# Revit family: Cooking_module_4_no of slots
name_source: partatom
category: Generic Models
revit_build: Autodesk Revit Architecture 2013 (Build: 20120221_2030(x64)
units: mm (PartAtom-declared; Revit-internal decimal feet)

## types (8) — shared parameters
D- benchtop = 700.01 mm
D- side box = 100 mm  [stored 0.328084 ft]
D- toe recess offset = 50 mm  [stored 0.164042 ft]
D-cooktop1 = 504.01 mm
D-cooktop2 = 504.01 mm
D-cooktop3 = 504.01 mm
D-cooktop4 = 504.01 mm
H- backpanel offset = 150 mm
H- benchtop = 900 mm
H- bottom of hood = 700 mm
H- total upto cabinets = 2100 mm
H-toe recess = 100 mm  [stored 0.328084 ft]
SS edging = BA-01
T- benchtop = 80 mm
W- back panel offset = 150 mm
W- benchtop waterfall = 80 mm
W- oven1 = 695 mm
W-hood3 cabinet = 1200 mm
W-oven2 = 695 mm
W-oven3 = 695 mm
W-oven4 = 695 mm
W-side box = 150 mm
back panel = PT-02
hood cabinets = PT-01
infills btwn ovens = PT-03
mdf = MDF
side boxes = PT-01
ss infills under oven = SS-01
toe recess = PT-03
waterfalls = PT-03

## per-type parameters (varying)
- Cooking_module_4: D-hood1 C/O=112.6 mm  [stored 0.369423 ft]; D-hood1 C/O offset from backpanel=200 mm  [stored 0.656168 ft]; D-hood1 cabinet=100 mm  [stored 0.328084 ft]; D-hood2 C/O=111.92 mm; D-hood2 C/O offset from backpanel=100 mm  [stored 0.328084 ft]; D-hood2 cabinet=100 mm  [stored 0.328084 ft]; D-hood3 C/O=184.92 mm; D-hood3 C/O offset from backpanel=100 mm  [stored 0.328084 ft]; D-hood3 cabinet=100 mm  [stored 0.328084 ft]; D-hood4 C/O=227.1 mm; D-hood4 C/O offset from backpanel=100 mm  [stored 0.328084 ft]; D-hood4 cabinet=100 mm  [stored 0.328084 ft]; H-oven1=603 mm; H-oven2=603 mm; H-oven3=603 mm; H-oven4=603 mm; No. of slots=0; W- benchtop=1205 mm  [stored 3.95341 ft]; W- offset oven1 frm benchtop left edge=252.5 mm; W-cooktop1=780 mm  [stored 2.55906 ft]; W-cooktop2=780 mm  [stored 2.55906 ft]; W-cooktop3=780 mm  [stored 2.55906 ft]; W-cooktop4=780 mm  [stored 2.55906 ft]; W-hood 2 cabinet=1200 mm; W-hood1 C/O=198.49 mm; W-hood1 cabinet=1200 mm; W-hood2 C/O=251.33 mm; W-hood3 C/O=280 mm; W-hood4 C/O=305.53 mm; W-offset slot2 frm benchtop left edge=1452.5 mm; W-offset slot3 frm bechtop left edge=2652.5 mm; W-offset slot4 frm benchtop left edge=3852.5 mm; inbuilt hood1=No; inbuilt hood2=No; inbuilt hood3=No; inbuilt hood4=No
- Cooking_module_4 2 2: D-hood1 C/O=112.3 mm; D-hood1 C/O offset from backpanel=200 mm  [stored 0.656168 ft]; D-hood1 cabinet=600 mm; D-hood2 C/O=111.92 mm; D-hood2 C/O offset from backpanel=200 mm  [stored 0.656168 ft]; D-hood2 cabinet=600 mm; D-hood3 C/O=184.92 mm; D-hood3 C/O offset from backpanel=100 mm  [stored 0.328084 ft]; D-hood3 cabinet=100 mm  [stored 0.328084 ft]; D-hood4 C/O=227.1 mm; D-hood4 C/O offset from backpanel=100 mm  [stored 0.328084 ft]; D-hood4 cabinet=100 mm  [stored 0.328084 ft]; H-oven1=596 mm; H-oven2=596 mm; H-oven3=596 mm; H-oven4=596 mm; No. of slots=0; W- benchtop=1205 mm  [stored 3.95341 ft]; W- offset oven1 frm benchtop left edge=243.26 mm; W-cooktop1=614 mm  [stored 2.01444 ft]; W-cooktop2=614 mm  [stored 2.01444 ft]; W-cooktop3=614 mm  [stored 2.01444 ft]; W-cooktop4=614 mm  [stored 2.01444 ft]; W-hood 2 cabinet=1200 mm; W-hood1 C/O=198.49 mm; W-hood1 cabinet=1200 mm; W-hood2 C/O=251.33 mm; W-hood3 C/O=280 mm; W-hood4 C/O=305.53 mm; W-offset slot2 frm benchtop left edge=1450 mm  [stored 4.75722 ft]; W-offset slot3 frm bechtop left edge=2652.5 mm; W-offset slot4 frm benchtop left edge=243 mm; inbuilt hood1=Yes; inbuilt hood2=Yes; inbuilt hood3=No; inbuilt hood4=No
- Cooking_module_4 3: D-hood1 C/O=372 mm  [stored 1.22047 ft]; D-hood1 C/O offset from backpanel=181 mm  [stored 0.593832 ft]; D-hood1 cabinet=100 mm  [stored 0.328084 ft]; D-hood2 C/O=372 mm  [stored 1.22047 ft]; D-hood2 C/O offset from backpanel=181 mm  [stored 0.593832 ft]; D-hood2 cabinet=100 mm  [stored 0.328084 ft]; D-hood3 C/O=372 mm  [stored 1.22047 ft]; D-hood3 C/O offset from backpanel=181 mm  [stored 0.593832 ft]; D-hood3 cabinet=100 mm  [stored 0.328084 ft]; D-hood4 C/O=372 mm  [stored 1.22047 ft]; D-hood4 C/O offset from backpanel=181 mm  [stored 0.593832 ft]; D-hood4 cabinet=100 mm  [stored 0.328084 ft]; H-oven1=603 mm; H-oven2=603 mm; H-oven3=603 mm; H-oven4=603 mm; No. of slots=2; W- benchtop=2405 mm; W- offset oven1 frm benchtop left edge=252.5 mm; W-cooktop1=780 mm  [stored 2.55906 ft]; W-cooktop2=780 mm  [stored 2.55906 ft]; W-cooktop3=780 mm  [stored 2.55906 ft]; W-cooktop4=780 mm  [stored 2.55906 ft]; W-hood 2 cabinet=1200 mm; W-hood1 C/O=532 mm  [stored 1.74541 ft]; W-hood1 cabinet=1200 mm; W-hood2 C/O=532 mm  [stored 1.74541 ft]; W-hood3 C/O=532 mm  [stored 1.74541 ft]; W-hood4 C/O=532 mm  [stored 1.74541 ft]; W-offset slot2 frm benchtop left edge=1452.5 mm; W-offset slot3 frm bechtop left edge=2652.5 mm; W-offset slot4 frm benchtop left edge=3852.5 mm; inbuilt hood1=No; inbuilt hood2=No; inbuilt hood3=No; inbuilt hood4=No
- Cooking_module_4 2: D-hood1 C/O=112.3 mm; D-hood1 C/O offset from backpanel=200 mm  [stored 0.656168 ft]; D-hood1 cabinet=100 mm  [stored 0.328084 ft]; D-hood2 C/O=111.92 mm; D-hood2 C/O offset from backpanel=200 mm  [stored 0.656168 ft]; D-hood2 cabinet=100 mm  [stored 0.328084 ft]; D-hood3 C/O=184.92 mm; D-hood3 C/O offset from backpanel=100 mm  [stored 0.328084 ft]; D-hood3 cabinet=100 mm  [stored 0.328084 ft]; D-hood4 C/O=227.1 mm; D-hood4 C/O offset from backpanel=100 mm  [stored 0.328084 ft]; D-hood4 cabinet=100 mm  [stored 0.328084 ft]; H-oven1=596 mm; H-oven2=596 mm; H-oven3=596 mm; H-oven4=596 mm; No. of slots=0; W- benchtop=1205 mm  [stored 3.95341 ft]; W- offset oven1 frm benchtop left edge=243.26 mm; W-cooktop1=614 mm  [stored 2.01444 ft]; W-cooktop2=614 mm  [stored 2.01444 ft]; W-cooktop3=614 mm  [stored 2.01444 ft]; W-cooktop4=614 mm  [stored 2.01444 ft]; W-hood 2 cabinet=1200 mm; W-hood1 C/O=198.49 mm; W-hood1 cabinet=1197.5 mm  [stored 3.92881 ft]; W-hood2 C/O=251.33 mm; W-hood3 C/O=280 mm; W-hood4 C/O=305.53 mm; W-offset slot2 frm benchtop left edge=1451.83 mm  [stored 4.76322 ft]; W-offset slot3 frm bechtop left edge=2652.5 mm; W-offset slot4 frm benchtop left edge=243 mm; inbuilt hood1=No; inbuilt hood2=No; inbuilt hood3=No; inbuilt hood4=No
- Cooking_module_4 2 4: D-hood1 C/O=112.3 mm; D-hood1 C/O offset from backpanel=200 mm  [stored 0.656168 ft]; D-hood1 cabinet=600 mm; D-hood2 C/O=400 mm  [stored 1.31234 ft]; D-hood2 C/O offset from backpanel=180 mm  [stored 0.590551 ft]; D-hood2 cabinet=100 mm  [stored 0.328084 ft]; D-hood3 C/O=184.92 mm; D-hood3 C/O offset from backpanel=100 mm  [stored 0.328084 ft]; D-hood3 cabinet=100 mm  [stored 0.328084 ft]; D-hood4 C/O=227.1 mm; D-hood4 C/O offset from backpanel=100 mm  [stored 0.328084 ft]; D-hood4 cabinet=100 mm  [stored 0.328084 ft]; H-oven1=596 mm; H-oven2=596 mm; H-oven3=596 mm; H-oven4=596 mm; No. of slots=0; W- benchtop=1205 mm  [stored 3.95341 ft]; W- offset oven1 frm benchtop left edge=243.26 mm; W-cooktop1=614 mm  [stored 2.01444 ft]; W-cooktop2=614 mm  [stored 2.01444 ft]; W-cooktop3=614 mm  [stored 2.01444 ft]; W-cooktop4=614 mm  [stored 2.01444 ft]; W-hood 2 cabinet=1200 mm; W-hood1 C/O=198.49 mm; W-hood1 cabinet=1197.5 mm  [stored 3.92881 ft]; W-hood2 C/O=500 mm  [stored 1.64042 ft]; W-hood3 C/O=280 mm; W-hood4 C/O=305.53 mm; W-offset slot2 frm benchtop left edge=1451.83 mm  [stored 4.76322 ft]; W-offset slot3 frm bechtop left edge=2652.5 mm; W-offset slot4 frm benchtop left edge=1451.83 mm  [stored 4.76322 ft]; inbuilt hood1=Yes; inbuilt hood2=No; inbuilt hood3=No; inbuilt hood4=No
- Cooking_module_4 2 3: D-hood1 C/O=112.3 mm; D-hood1 C/O offset from backpanel=200 mm  [stored 0.656168 ft]; D-hood1 cabinet=600 mm; D-hood2 C/O=111.92 mm; D-hood2 C/O offset from backpanel=200 mm  [stored 0.656168 ft]; D-hood2 cabinet=600 mm; D-hood3 C/O=184.92 mm; D-hood3 C/O offset from backpanel=100 mm  [stored 0.328084 ft]; D-hood3 cabinet=600 mm; D-hood4 C/O=227.1 mm; D-hood4 C/O offset from backpanel=100 mm  [stored 0.328084 ft]; D-hood4 cabinet=600 mm; H-oven1=596 mm; H-oven2=596 mm; H-oven3=596 mm; H-oven4=596 mm; No. of slots=0; W- benchtop=1205 mm  [stored 3.95341 ft]; W- offset oven1 frm benchtop left edge=243.26 mm; W-cooktop1=614 mm  [stored 2.01444 ft]; W-cooktop2=614 mm  [stored 2.01444 ft]; W-cooktop3=614 mm  [stored 2.01444 ft]; W-cooktop4=614 mm  [stored 2.01444 ft]; W-hood 2 cabinet=1200 mm; W-hood1 C/O=198.49 mm; W-hood1 cabinet=1197.5 mm  [stored 3.92881 ft]; W-hood2 C/O=251.33 mm; W-hood3 C/O=280 mm; W-hood4 C/O=305.53 mm; W-offset slot2 frm benchtop left edge=1451.83 mm  [stored 4.76322 ft]; W-offset slot3 frm bechtop left edge=2652.5 mm; W-offset slot4 frm benchtop left edge=243 mm; inbuilt hood1=Yes; inbuilt hood2=Yes; inbuilt hood3=Yes; inbuilt hood4=Yes
- Cooking_module_4_1: D-hood1 C/O=112.3 mm; D-hood1 C/O offset from backpanel=200 mm  [stored 0.656168 ft]; D-hood1 cabinet=600 mm; D-hood2 C/O=400 mm  [stored 1.31234 ft]; D-hood2 C/O offset from backpanel=180 mm  [stored 0.590551 ft]; D-hood2 cabinet=100 mm  [stored 0.328084 ft]; D-hood3 C/O=184.92 mm; D-hood3 C/O offset from backpanel=100 mm  [stored 0.328084 ft]; D-hood3 cabinet=100 mm  [stored 0.328084 ft]; D-hood4 C/O=227.1 mm; D-hood4 C/O offset from backpanel=100 mm  [stored 0.328084 ft]; D-hood4 cabinet=100 mm  [stored 0.328084 ft]; H-oven1=596 mm; H-oven2=596 mm; H-oven3=596 mm; H-oven4=596 mm; No. of slots=0; W- benchtop=1205 mm  [stored 3.95341 ft]; W- offset oven1 frm benchtop left edge=243.26 mm; W-cooktop1=614 mm  [stored 2.01444 ft]; W-cooktop2=614 mm  [stored 2.01444 ft]; W-cooktop3=614 mm  [stored 2.01444 ft]; W-cooktop4=614 mm  [stored 2.01444 ft]; W-hood 2 cabinet=1205 mm  [stored 3.95341 ft]; W-hood1 C/O=198.49 mm; W-hood1 cabinet=1197.5 mm  [stored 3.92881 ft]; W-hood2 C/O=500 mm  [stored 1.64042 ft]; W-hood3 C/O=280 mm; W-hood4 C/O=305.53 mm; W-offset slot2 frm benchtop left edge=1451.83 mm  [stored 4.76322 ft]; W-offset slot3 frm bechtop left edge=0 mm  [stored 0 ft]; W-offset slot4 frm benchtop left edge=0 mm  [stored 0 ft]; inbuilt hood1=Yes; inbuilt hood2=No; inbuilt hood3=No; inbuilt hood4=No
- Cooking_module_4_3: D-hood1 C/O=112.3 mm; D-hood1 C/O offset from backpanel=200 mm  [stored 0.656168 ft]; D-hood1 cabinet=600 mm; D-hood2 C/O=400 mm  [stored 1.31234 ft]; D-hood2 C/O offset from backpanel=180 mm  [stored 0.590551 ft]; D-hood2 cabinet=600 mm; D-hood3 C/O=184.92 mm; D-hood3 C/O offset from backpanel=100 mm  [stored 0.328084 ft]; D-hood3 cabinet=600 mm; D-hood4 C/O=227.1 mm; D-hood4 C/O offset from backpanel=100 mm  [stored 0.328084 ft]; D-hood4 cabinet=100 mm  [stored 0.328084 ft]; H-oven1=596 mm; H-oven2=596 mm; H-oven3=596 mm; H-oven4=596 mm; No. of slots=0; W- benchtop=1205 mm  [stored 3.95341 ft]; W- offset oven1 frm benchtop left edge=243.26 mm; W-cooktop1=614 mm  [stored 2.01444 ft]; W-cooktop2=614 mm  [stored 2.01444 ft]; W-cooktop3=614 mm  [stored 2.01444 ft]; W-cooktop4=614 mm  [stored 2.01444 ft]; W-hood 2 cabinet=1200 mm; W-hood1 C/O=198.49 mm; W-hood1 cabinet=1197.5 mm  [stored 3.92881 ft]; W-hood2 C/O=500 mm  [stored 1.64042 ft]; W-hood3 C/O=280 mm; W-hood4 C/O=305.53 mm; W-offset slot2 frm benchtop left edge=1451.83 mm  [stored 4.76322 ft]; W-offset slot3 frm bechtop left edge=2652.5 mm; W-offset slot4 frm benchtop left edge=2652.5 mm; inbuilt hood1=Yes; inbuilt hood2=Yes; inbuilt hood3=Yes; inbuilt hood4=No

note: [stored X ft] marks values corroborated as IEEE doubles in the binary element streams (Revit-internal decimal feet)

## geometry (parser evidence)
native form markers: Blend x10, Sweep x1
no freeform markers — native parametric forms only
